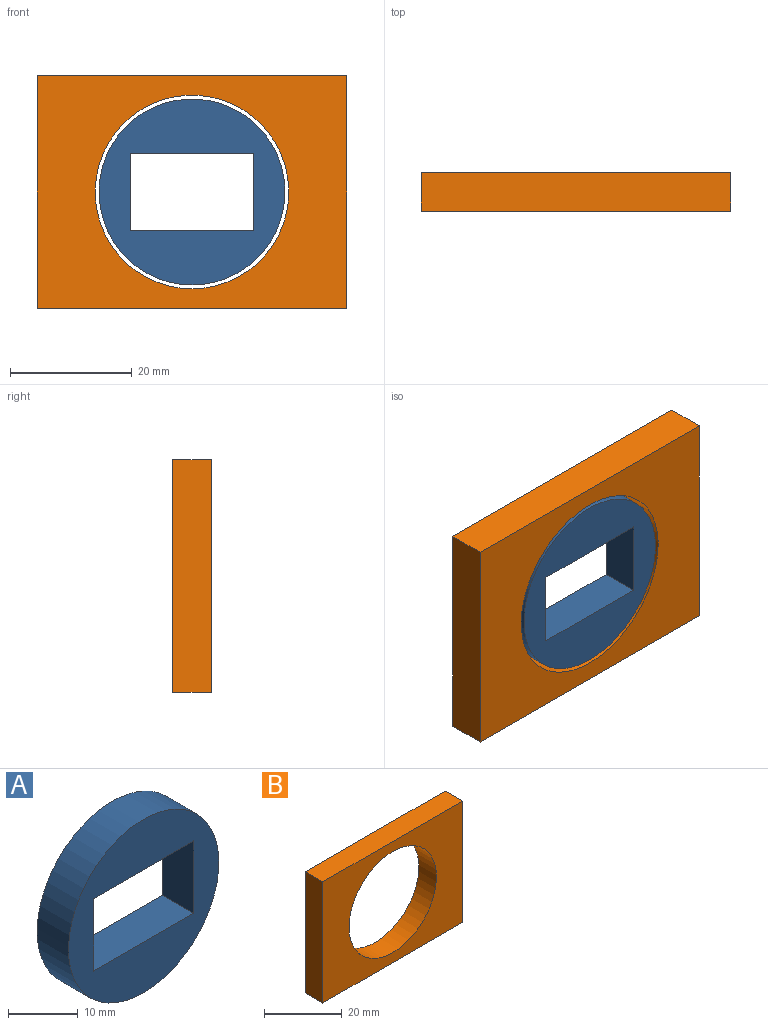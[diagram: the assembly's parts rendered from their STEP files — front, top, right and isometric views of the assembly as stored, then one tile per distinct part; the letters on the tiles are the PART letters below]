
ASSEMBLY  parts=2 mates=1
PART A: 7 faces, bbox 30.5x6.4x30.5 mm
  f0: plane 12.7x6.35mm, normal (1,0,0), area 80.6mm2, adj f1,f3,f5,f6
  f1: plane 20.32x6.35mm, normal (0,0,-1), area 129mm2, adj f0,f2,f5,f6
  f2: plane 12.7x6.35mm, normal (-1,0,0), area 80.6mm2, adj f1,f3,f5,f6
  f3: plane 20.32x6.35mm, normal (0,0,1), area 129mm2, adj f0,f2,f5,f6
  f4: cylinder r=15.24mm len=30.48mm, axis (0,1,0), area 608mm2, adj f5,f6
  f5: plane 30.48x30.48mm, normal (0,-1,0), area 471.6mm2, adj f0,f1,f2,f3,f4
  f6: plane 30.48x30.48mm, normal (0,1,0), area 471.6mm2, adj f0,f1,f2,f3,f4
PART B: 7 faces, bbox 50.8x6.4x38.1 mm
  f0: plane 50.8x6.35mm, normal (0,0,1), area 322.6mm2, adj f1,f3,f4,f5
  f1: plane 38.1x6.35mm, normal (-1,0,0), area 241.9mm2, adj f0,f2,f4,f5
  f2: plane 50.8x6.35mm, normal (0,0,-1), area 322.6mm2, adj f1,f3,f4,f5
  f3: plane 38.1x6.35mm, normal (1,0,0), area 241.9mm2, adj f0,f2,f4,f5
  f4: plane 50.8x38.1mm, normal (0,-1,0), area 1143.7mm2, adj f0,f1,f2,f3,f6
  f5: plane 50.8x38.1mm, normal (0,1,0), area 1143.7mm2, adj f0,f1,f2,f3,f6
  f6: cylinder r=15.88mm len=31.75mm, axis (0,-1,0), area 633.4mm2, adj f4,f5
PLACE A t=(-8.8,3.08,67.96)mm
PLACE B t=(-18.31,3.08,-5.89)mm
MATE fastened A.f4 <-> B.f6  axis (0,-1,0) through (19.55,-3.27,-17.07)mm
